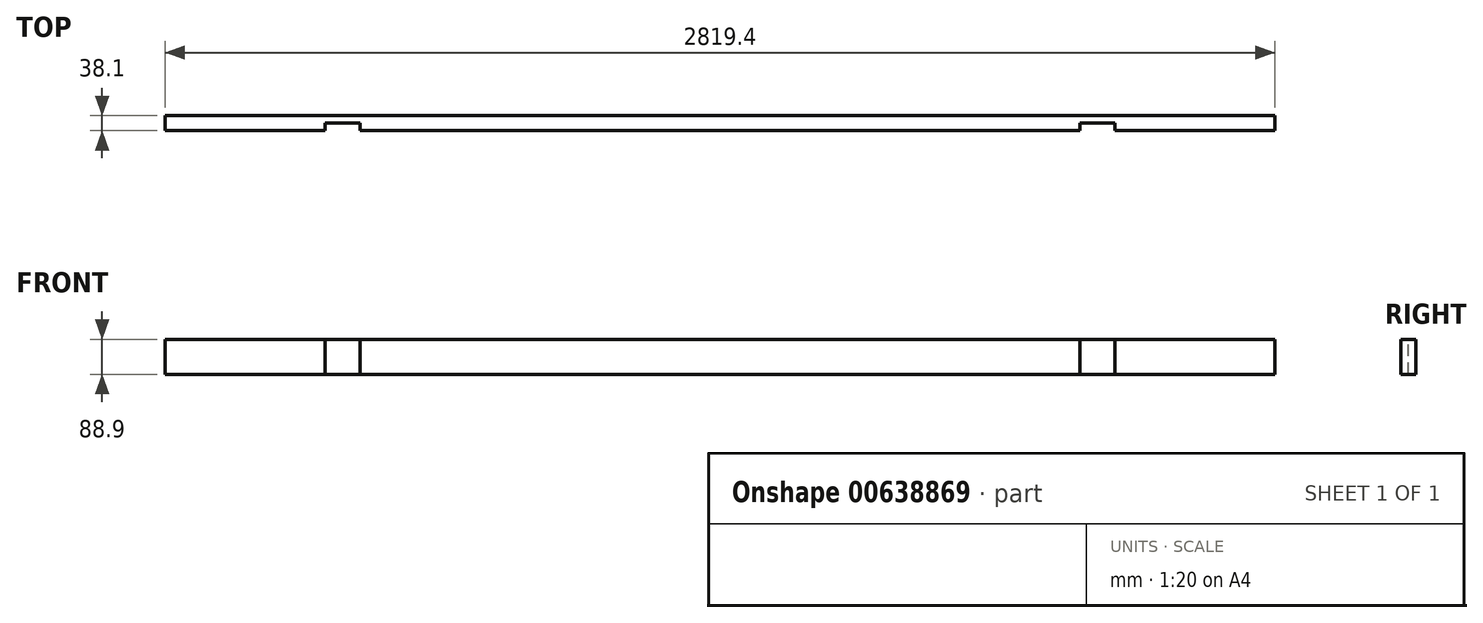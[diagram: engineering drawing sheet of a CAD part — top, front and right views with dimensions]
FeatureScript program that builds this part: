
annotation { "Feature Type Name" : "Feature", "Feature Type Description" : "" }
export const myFeature = defineFeature(function(context is Context, id is Id, definition is map)
    precondition{}
    {
        {
            var Q0;
            Q0=qCreatedBy(makeId("Right.planeOp"),FACE);
            var sketch = newSketch(context, id + "F0", { "sketchPlane" : qUnion([Q0])});
            skLineSegment(sketch, "E0.bottom", {"start": v(19.05, 44.45) * mm, "end": v(-19.05, 44.45) * mm});
            skLineSegment(sketch, "E0.top", {"start": v(19.05, -44.45) * mm, "end": v(-19.05, -44.45) * mm});
            skLineSegment(sketch, "E0.left", {"start": v(19.05, 44.45) * mm, "end": v(19.05, -44.45) * mm});
            skLineSegment(sketch, "E0.right", {"start": v(-19.05, 44.45) * mm, "end": v(-19.05, -44.45) * mm});
            skPoint(sketch, "E0.middle", {"position": v(0, 0) * mm});
            skSolve(sketch);
        }
        {
            var Q0;
            Q0=qSketchRegion(id+"F0",true);
            extrude(context, id + "F1", {"entities" : qUnion([Q0]), "depth" : 1409.7 * mm, "offsetDistance" : 25.4 * mm});
        }
        {
            var Q0;
            {var subQ0=makeQuery(id+"F1.opExtrude","SWEPT_FACE",FACE,{"disambiguationData":[OSD([sQuery(id+"F0.wireOp",EDGE,"E0.bottom")])]});Q0=makeQuery(id+"F4.boolean.opBoolean","MERGE",FACE,{"derivedFrom":[subQ0,makeQuery(id+"F4.opPattern","COPY",FACE,{"derivedFrom":subQ0,"instanceName":"1"})]});}
            var sketch = newSketch(context, id + "F2", { "sketchPlane" : qUnion([Q0])});
            skLineSegment(sketch, "E1.bottom", {"start": v(1003.3, -19.05) * mm, "end": v(914.4, -19.05) * mm});
            skLineSegment(sketch, "E1.top", {"start": v(1003.3, 0) * mm, "end": v(914.4, 0) * mm});
            skLineSegment(sketch, "E1.left", {"start": v(1003.3, -19.05) * mm, "end": v(1003.3, 0) * mm});
            skLineSegment(sketch, "E1.right", {"start": v(914.4, -19.05) * mm, "end": v(914.4, 0) * mm});
            skSolve(sketch);
        }
        {
            var Q0;
            Q0=qSketchRegion(id+"F2",true);
            extrude(context, id + "F3", {"entities" : qUnion([Q0]), "operationType" : NewBodyOperationType.REMOVE, "endBound" : BoundingType.UP_TO_NEXT, "oppositeDirection" : true, "depth" : 25.4 * mm, "offsetDistance" : 25.4 * mm});
        }
        {
            var Q0;
            Q0=makeQuery(id+"F1.opExtrude","SWEPT_BODY",BODY,{"disambiguationData":[OSD([sQuery(id+"F0.wireOp",EDGE,"E0.bottom"),sQuery(id+"F0.wireOp",EDGE,"E0.top"),sQuery(id+"F0.wireOp",EDGE,"E0.left"),sQuery(id+"F0.wireOp",EDGE,"E0.right")])]});
            var Q1;
            Q1=qCreatedBy(makeId("Right.planeOp"),FACE);
            mirror(context, id + "F4", {"operationType" : NewBodyOperationType.ADD, "entities" : qUnion([Q0]), "mirrorPlane" : qUnion([Q1])});
        }
    });
